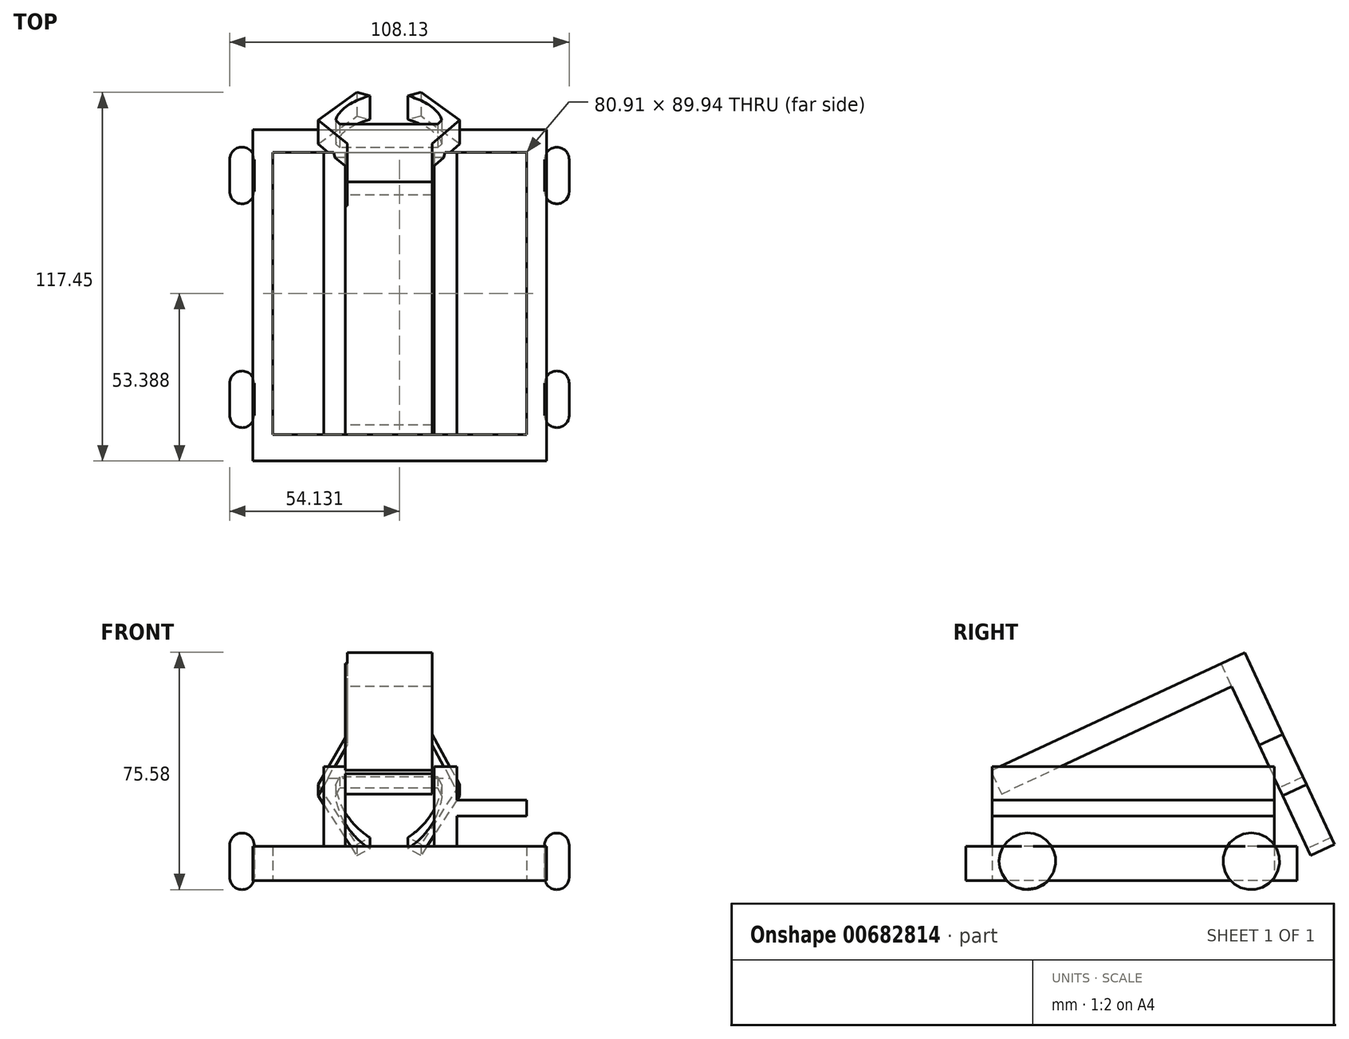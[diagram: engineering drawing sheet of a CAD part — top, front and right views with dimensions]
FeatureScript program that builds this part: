
annotation { "Feature Type Name" : "Feature", "Feature Type Description" : "" }
export const myFeature = defineFeature(function(context is Context, id is Id, definition is map)
    precondition{}
    {
        {
            var Q0;
            Q0=qCreatedBy(makeId("Top.planeOp"),FACE);
            var sketch = newSketch(context, id + "F0", { "sketchPlane" : qUnion([Q0])});
            skLineSegment(sketch, "E0.bottom", {"start": v(-46.47, 55.2) * mm, "end": v(47.07, 55.2) * mm});
            skLineSegment(sketch, "E0.top", {"start": v(-46.47, -50.38) * mm, "end": v(47.07, -50.38) * mm});
            skLineSegment(sketch, "E0.left", {"start": v(-46.47, 55.2) * mm, "end": v(-46.47, -50.38) * mm});
            skLineSegment(sketch, "E0.right", {"start": v(47.07, 55.2) * mm, "end": v(47.07, -50.38) * mm});
            skLineSegment(sketch, "E1.bottom", {"start": v(-40.16, 47.98) * mm, "end": v(40.76, 47.98) * mm});
            skLineSegment(sketch, "E1.top", {"start": v(-40.16, -41.96) * mm, "end": v(40.76, -41.96) * mm});
            skLineSegment(sketch, "E1.left", {"start": v(-40.16, 47.98) * mm, "end": v(-40.16, -41.96) * mm});
            skLineSegment(sketch, "E1.right", {"start": v(40.76, 47.98) * mm, "end": v(40.76, -41.96) * mm});
            skLineSegment(sketch, "E2.bottom", {"start": v(-23.91, -41.96) * mm, "end": v(-17, -41.96) * mm});
            skLineSegment(sketch, "E2.top", {"start": v(-23.91, 47.98) * mm, "end": v(-17, 47.98) * mm});
            skLineSegment(sketch, "E2.left", {"start": v(-23.91, -41.96) * mm, "end": v(-23.91, 47.98) * mm});
            skLineSegment(sketch, "E2.right", {"start": v(-17, -41.96) * mm, "end": v(-17, 47.98) * mm});
            skLineSegment(sketch, "E3.bottom", {"start": v(11.28, 47.98) * mm, "end": v(18.5, 47.98) * mm});
            skLineSegment(sketch, "E3.top", {"start": v(11.28, -41.96) * mm, "end": v(18.5, -41.96) * mm});
            skLineSegment(sketch, "E3.left", {"start": v(11.28, 47.98) * mm, "end": v(11.28, -41.96) * mm});
            skLineSegment(sketch, "E3.right", {"start": v(18.5, 47.98) * mm, "end": v(18.5, -41.96) * mm});
            skSolve(sketch);
        }
        {
            var Q0;
            Q0=makeQuery(id+"F0.imprint","IMPRINT",FACE,{"disambiguationData":[TD([[makeQuery(id+"F0.imprint","IMPRINT",EDGE,{"derivedFrom":sQuery(id+"F0.wireOp",EDGE,"E0.bottom")}),-1.0]])]});
            var Q1;
            Q1=makeQuery(id+"F0.imprint","IMPRINT",FACE,{"disambiguationData":[TD([[makeQuery(id+"F0.imprint","IMPRINT",EDGE,{"derivedFrom":sQuery(id+"F0.wireOp",EDGE,"E2.bottom")}),1.0]])]});
            var Q2;
            Q2=makeQuery(id+"F0.imprint","IMPRINT",FACE,{"disambiguationData":[TD([[makeQuery(id+"F0.imprint","IMPRINT",EDGE,{"derivedFrom":sQuery(id+"F0.wireOp",EDGE,"E3.bottom")}),-1.0]])]});
            extrude(context, id + "F1", {"entities" : qUnion([Q0, Q1, Q2]), "depth" : 10.92 * mm, "offsetDistance" : 25.4 * mm});
        }
        {
            var Q0;
            Q0=qCreatedBy(makeId("Front.planeOp"),FACE);
            cPlane(context, id + "F2", {"entities" : qUnion([Q0]), "cplaneType" : CPlaneType.OFFSET, "offset" : 30.73 * mm, "width" : 152.4 * mm, "height" : 152.4 * mm});
        }
        {
            var Q0;
            Q0=qCreatedBy(id+"F2.planeOp",FACE);
            var sketch = newSketch(context, id + "F3", { "sketchPlane" : qUnion([Q0])});
            skLineSegment(sketch, "E4", {"start": v(-46.01, 6.17) * mm, "end": v(56.7, 6.17) * mm});
            skArc(sketch, "E5", {"start": v(-46.01, 11.28) * mm, "mid": v(-49.92, 15.19) * mm, "end": v(-53.83, 11.28) * mm});
            skLineSegment(sketch, "E6", {"start": v(-53.83, 11.28) * mm, "end": v(-53.83, 6.17) * mm});
            skLineSegment(sketch, "E7", {"start": v(-46.01, 11.28) * mm, "end": v(-46.01, 6.17) * mm});
            skPoint(sketch, "E8.orphan", {"position": v(-50.68, 6.17) * mm});
            skArc(sketch, "E9", {"start": v(54.3, 11.28) * mm, "mid": v(50.4, 15.19) * mm, "end": v(46.48, 11.28) * mm});
            skLineSegment(sketch, "E10", {"start": v(46.48, 11.28) * mm, "end": v(46.48, 6.17) * mm});
            skLineSegment(sketch, "E11", {"start": v(54.3, 11.28) * mm, "end": v(54.3, 6.17) * mm});
            skLineSegment(sketch, "E12", {"start": v(-46.01, 6.17) * mm, "end": v(-53.83, 6.17) * mm});
            skSolve(sketch);
        }
        {
            var Q0;
            Q0=makeQuery(id+"F3.imprint","IMPRINT",FACE,{"disambiguationData":[TD([[makeQuery(id+"F3.imprint","IMPRINT",EDGE,{"derivedFrom":sQuery(id+"F3.wireOp",EDGE,"E5")}),1.0]])]});
            var Q1;
            Q1=makeQuery(id+"F3.imprint","IMPRINT",FACE,{"disambiguationData":[TD([[makeQuery(id+"F3.imprint","IMPRINT",EDGE,{"derivedFrom":sQuery(id+"F3.wireOp",EDGE,"E9")}),1.0]])]});
            var Q2;
            Q2=sQuery(id+"F3.wireOp",EDGE,"E4");
            revolve(context, id + "F4", {"surfaceOperationType" : NewSurfaceOperationType.NEW, "entities" : qUnion([Q0, Q1]), "axis" : qUnion([Q2]), "revolveType" : RevolveType.FULL});
        }
        {
            var Q0;
            {var subQ0=sQuery(id+"F0.wireOp",EDGE,"E0.bottom");var subQ10=sQuery(id+"F0.wireOp",EDGE,"E0.left");Q0=makeQuery(id+"F4.boolean.opBoolean","SPLIT",FACE,{"disambiguationData":[TD([makeQuery(id+"F1.opExtrude","SWEPT_FACE",FACE,{"disambiguationData":[OSD([subQ0])]})])],"derivedFrom":makeQuery(id+"F1.opExtrude","SWEPT_FACE",FACE,{"disambiguationData":[OSD([subQ10])]})});}
            var sketch = newSketch(context, id + "F5", { "sketchPlane" : qUnion([Q0])});
            skPoint(sketch, "E13", {"position": v(-40.64, 10.92) * mm});
            skPoint(sketch, "E14", {"position": v(30.68, 10.92) * mm});
            skSolve(sketch);
        }
        {
            var Q0;
            Q0=makeQuery(id+"F4.opRevolve","SWEPT_BODY",BODY,{"disambiguationData":[OSD([sQuery(id+"F3.wireOp",EDGE,"E5"),sQuery(id+"F3.wireOp",EDGE,"E6"),sQuery(id+"F3.wireOp",EDGE,"E7"),sQuery(id+"F3.wireOp",EDGE,"E12")])]});
            var Q1;
            Q1=makeQuery(id+"F4.opRevolve","SWEPT_BODY",BODY,{"disambiguationData":[OSD([sQuery(id+"F3.wireOp",EDGE,"E4"),sQuery(id+"F3.wireOp",EDGE,"E9"),sQuery(id+"F3.wireOp",EDGE,"E10"),sQuery(id+"F3.wireOp",EDGE,"E11")])]});
            var Q2;
            Q2=sQuery(id+"F5.wireOp",VERTEX,"E14");
            var Q3;
            Q3=sQuery(id+"F5.wireOp",VERTEX,"E13");
            transform(context, id + "F6", {"entities" : qUnion([Q0, Q1]), "transformType" : TransformType.TRANSLATION_ENTITY, "oppositeDirectionEntity" : false, "transformLine" : qUnion([Q2, Q3]), "makeCopy" : true});
        }
        {
            var Q0;
            Q0=makeQuery(id+"F1.opExtrude","CAP_FACE",FACE,{"disambiguationData":[OSD([sQuery(id+"F0.wireOp",EDGE,"E0.bottom"),sQuery(id+"F0.wireOp",EDGE,"E0.top"),sQuery(id+"F0.wireOp",EDGE,"E0.left"),sQuery(id+"F0.wireOp",EDGE,"E0.right"),sQuery(id+"F0.wireOp",EDGE,"E1.bottom"),sQuery(id+"F0.wireOp",EDGE,"E1.top"),sQuery(id+"F0.wireOp",EDGE,"E1.left"),sQuery(id+"F0.wireOp",EDGE,"E1.right"),sQuery(id+"F0.wireOp",EDGE,"E2.left"),sQuery(id+"F0.wireOp",EDGE,"E2.right"),sQuery(id+"F0.wireOp",EDGE,"E3.left"),sQuery(id+"F0.wireOp",EDGE,"E3.right")])],"isStart":false});
            var sketch = newSketch(context, id + "F7", { "sketchPlane" : qUnion([Q0])});
            skLineSegment(sketch, "E15.bottom", {"start": v(-23.91, -41.96) * mm, "end": v(-17, -41.96) * mm});
            skLineSegment(sketch, "E15.top", {"start": v(-23.91, 47.98) * mm, "end": v(-17, 47.98) * mm});
            skLineSegment(sketch, "E15.left", {"start": v(-23.91, -41.96) * mm, "end": v(-23.91, 47.98) * mm});
            skLineSegment(sketch, "E15.right", {"start": v(-17, -41.96) * mm, "end": v(-17, 47.98) * mm});
            skLineSegment(sketch, "E16.bottom", {"start": v(11.28, 47.98) * mm, "end": v(18.5, 47.98) * mm});
            skLineSegment(sketch, "E16.top", {"start": v(11.28, -41.96) * mm, "end": v(18.5, -41.96) * mm});
            skLineSegment(sketch, "E16.left", {"start": v(11.28, 47.98) * mm, "end": v(11.28, -41.96) * mm});
            skLineSegment(sketch, "E16.right", {"start": v(18.5, 47.98) * mm, "end": v(18.5, -41.96) * mm});
            skLineSegment(sketch, "E17.bottom", {"start": v(18.5, -41.96) * mm, "end": v(40.76, -41.96) * mm});
            skLineSegment(sketch, "E17.top", {"start": v(18.5, 47.98) * mm, "end": v(40.76, 47.98) * mm});
            skLineSegment(sketch, "E17.left", {"start": v(18.5, -41.96) * mm, "end": v(18.5, 47.98) * mm});
            skLineSegment(sketch, "E17.right", {"start": v(40.76, -41.96) * mm, "end": v(40.76, 47.98) * mm});
            skSolve(sketch);
        }
        {
            var Q0;
            Q0=makeQuery(id+"F7.imprint","IMPRINT",FACE,{"disambiguationData":[TD([[makeQuery(id+"F7.imprint","IMPRINT",EDGE,{"derivedFrom":sQuery(id+"F7.wireOp",EDGE,"E15.bottom")}),1.0]])]});
            var Q1;
            Q1=makeQuery(id+"F7.imprint","IMPRINT",FACE,{"disambiguationData":[TD([[makeQuery(id+"F7.imprint","IMPRINT",EDGE,{"derivedFrom":sQuery(id+"F7.wireOp",EDGE,"E16.bottom")}),-1.0]])]});
            extrude(context, id + "F8", {"entities" : qUnion([Q0, Q1]), "operationType" : NewBodyOperationType.ADD, "depth" : 25.4 * mm, "offsetDistance" : 25.4 * mm});
        }
        {
            var Q0;
            Q0=makeQuery(id+"F7.imprint","IMPRINT",FACE,{"disambiguationData":[TD([[makeQuery(id+"F7.imprint","IMPRINT",EDGE,{"derivedFrom":sQuery(id+"F7.wireOp",EDGE,"E17.bottom")}),1.0]])]});
            extrude(context, id + "F9", {"entities" : qUnion([Q0]), "operationType" : NewBodyOperationType.ADD, "depth" : 14.73 * mm, "offsetDistance" : 25.4 * mm, "hasSecondDirection" : true, "secondDirectionOppositeDirection" : false, "secondDirectionDepth" : 9.65 * mm});
        }
        {
            var Q0;
            Q0=makeQuery(id+"F8.boolean.opBoolean","MERGE",FACE,{"derivedFrom":[makeQuery(id+"F1.opExtrude","SWEPT_FACE",FACE,{"disambiguationData":[OSD([sQuery(id+"F0.wireOp",EDGE,"E2.right")])]}),makeQuery(id+"F8.opExtrude","SWEPT_FACE",FACE,{"disambiguationData":[OSD([sQuery(id+"F7.wireOp",EDGE,"E15.right")])]})]});
            var sketch = newSketch(context, id + "F10", { "sketchPlane" : qUnion([Q0])});
            skLineSegment(sketch, "E18.bottom", {"start": v(-42.4, 34.98) * mm, "end": v(30.93, 69.18) * mm});
            skLineSegment(sketch, "E18.top", {"start": v(-38.97, 27.62) * mm, "end": v(34.36, 61.82) * mm});
            skLineSegment(sketch, "E18.left", {"start": v(-42.4, 34.98) * mm, "end": v(-38.97, 27.62) * mm});
            skLineSegment(sketch, "E18.right", {"start": v(30.93, 69.18) * mm, "end": v(34.36, 61.82) * mm});
            skSolve(sketch);
        }
        {
            var Q0;
            {var subQ0=sQuery(id+"F10.wireOp",EDGE,"E18.right");Q0=makeQuery(id+"F10.imprint","IMPRINT",FACE,{"disambiguationData":[TD([[makeQuery(id+"F10.imprint","IMPRINT",EDGE,{"derivedFrom":subQ0}),-1.0]])]});}
            var Q1;
            {var subQ4=sQuery(id+"F10.wireOp",EDGE,"E18.left");var subQ6=sQuery(id+"F10.wireOp",EDGE,"E18.top");var subQ7=makeQuery(id+"F10.imprint","INTERSECT",VERTEX,{"derivedFrom":[subQ6,subQ4]});Q1=makeQuery(id+"F10.imprint","IMPRINT",FACE,{"disambiguationData":[TD([[makeQuery(id+"F10.imprint","IMPRINT",EDGE,{"disambiguationData":[TD([[subQ7,-1.0]])],"derivedFrom":subQ6}),1.0]])]});}
            extrude(context, id + "F11", {"entities" : qUnion([Q0, Q1]), "operationType" : NewBodyOperationType.ADD, "depth" : 27.7 * mm, "offsetDistance" : 25.4 * mm});
        }
        {
            var Q0;
            Q0=makeQuery(id+"F11.opExtrude","SWEPT_FACE",FACE,{"disambiguationData":[OSD([sQuery(id+"F10.wireOp",EDGE,"E18.right")])]});
            var sketch = newSketch(context, id + "F12", { "sketchPlane" : qUnion([Q0])});
            skLineSegment(sketch, "E19.bottom", {"start": v(-10.7, 49.62) * mm, "end": v(16.4, 49.62) * mm});
            skLineSegment(sketch, "E19.left", {"start": v(-10.7, 49.62) * mm, "end": v(-10.7, 20.89) * mm});
            skLineSegment(sketch, "E19.right", {"start": v(16.4, 49.62) * mm, "end": v(16.4, 20.89) * mm});
            skLineSegment(sketch, "E20", {"start": v(-10.7, 20.89) * mm, "end": v(-19.4, 3.14) * mm});
            skLineSegment(sketch, "E21", {"start": v(-19.4, 3.14) * mm, "end": v(-7.06, -17.92) * mm});
            skLineSegment(sketch, "E22", {"start": v(-7.06, -17.92) * mm, "end": v(-2.88, -15.47) * mm});
            skLineSegment(sketch, "E23", {"start": v(-13.78, 3.14) * mm, "end": v(-12.44, 5.87) * mm});
            skArc(sketch, "E24", {"start": v(-13.78, 3.14) * mm, "mid": v(-10.34, -7.34) * mm, "end": v(-2.88, -15.47) * mm});
            skLineSegment(sketch, "E25.MirrorCS", {"start": v(13.37, -17.92) * mm, "end": v(9.18, -15.47) * mm});
            skArc(sketch, "E26.MirrorCS", {"start": v(20.08, 3.14) * mm, "mid": v(16.64, -7.34) * mm, "end": v(9.18, -15.47) * mm});
            skLineSegment(sketch, "E27.MirrorCS", {"start": v(25.7, 3.14) * mm, "end": v(13.37, -17.92) * mm});
            skLineSegment(sketch, "E28.MirrorCS", {"start": v(20.08, 3.14) * mm, "end": v(18.74, 5.87) * mm});
            skLineSegment(sketch, "E29.MirrorCS", {"start": v(16.4, 20.89) * mm, "end": v(25.7, 3.14) * mm});
            skLineSegment(sketch, "E30", {"start": v(-12.44, 5.87) * mm, "end": v(18.74, 5.87) * mm});
            skPoint(sketch, "E31.orphan", {"position": v(-18.06, 5.87) * mm});
            skSolve(sketch);
        }
        {
            var Q0;
            {var subQ3=sQuery(id+"F12.wireOp",EDGE,"E20");Q0=makeQuery(id+"F12.imprint","IMPRINT",FACE,{"disambiguationData":[TD([[makeQuery(id+"F12.imprint","IMPRINT",EDGE,{"derivedFrom":subQ3}),1.0]])]});}
            var Q1;
            {var subQ0=sQuery(id+"F12.wireOp",EDGE,"E19.bottom");Q1=makeQuery(id+"F12.imprint","IMPRINT",FACE,{"disambiguationData":[TD([[makeQuery(id+"F12.imprint","IMPRINT",EDGE,{"derivedFrom":subQ0}),-1.0]])]});}
            extrude(context, id + "F13", {"entities" : qUnion([Q0, Q1]), "operationType" : NewBodyOperationType.ADD, "depth" : 8.38 * mm, "offsetDistance" : 25.4 * mm});
        }
    });
